# Revit family: NLRS_27_GM_LIB_GI_MR
name_source: partatom
category: Generic Models
revit_build: Autodesk Revit 2017 (Build: 20190507_1515(x64)
units: mm (PartAtom-declared; Revit-internal decimal feet)

## family parameters
Can host rebar = No
Cut with Voids When Loaded = Yes
Part Type = Normal
Room Calculation Point = No
Round Connector Dimension = Use Diameter
Shared = No

## types (18) — shared parameters
01_kraal = No
02_Trim = Yes
03_druppel = Yes
Assembly Code = 27.16
Description = GI Goot
IfcExportAs = IfcFlowsegment
Manufacturer = Meilof Riks
Model = GI
NLRS_C_Binnenbak = RAL 9010
NLRS_C_Materiaal = RAL 9010
Type Image = <None>
URL = https://www.meilofriks.nl
Vorm_Goot_L = 01 : 2_←_Hoek_L
Vorm_Goot_L-R = 01 : 4_↔_Hoek_L-R
Vorm_goot_R = 01 : 3_→_Hoek_R

## per-type parameters (varying)
| type | Breedte_goot | Breedte_goot_hoek | Diepte_bak | Hoogte_AK | Hoogte_VK | Set_Diepte_bak | set_Hoogte_AK |
| GI S280A | 280 mm  [stored 0.918635 ft] | 280 mm  [stored 0.918635 ft] | 87 mm  [stored 0.285433 ft] | 197 mm | 168 mm | 87 mm  [stored 0.285433 ft] | 197 mm |
| GI S310A | 310 mm  [stored 1.01706 ft] | 310 mm  [stored 1.01706 ft] | 74 mm  [stored 0.242782 ft] | 179 mm  [stored 0.58727 ft] | 154 mm  [stored 0.505249 ft] | 74 mm  [stored 0.242782 ft] | 179 mm  [stored 0.58727 ft] |
| GI S365A | 365 mm  [stored 1.19751 ft] | 365 mm  [stored 1.19751 ft] | 95 mm | 204 mm | 176 mm | 95 mm | 204 mm |
| GI S400A | 400 mm  [stored 1.31234 ft] | 400 mm  [stored 1.31234 ft] | 78 mm  [stored 0.255906 ft] | 186 mm  [stored 0.610236 ft] | 157 mm  [stored 0.515092 ft] | 78 mm  [stored 0.255906 ft] | 186 mm  [stored 0.610236 ft] |
| GI S500A | 500 mm  [stored 1.64042 ft] | 500 mm  [stored 1.64042 ft] | 78 mm  [stored 0.255906 ft] | 186 mm  [stored 0.610236 ft] | 157 mm  [stored 0.515092 ft] | 78 mm  [stored 0.255906 ft] | 186 mm  [stored 0.610236 ft] |
| GI S280B | 280 mm  [stored 0.918635 ft] | 280 mm  [stored 0.918635 ft] | 87 mm  [stored 0.285433 ft] | 222 mm | 193 mm | 87 mm  [stored 0.285433 ft] | 222 mm |
| GI S280C | 280 mm  [stored 0.918635 ft] | 280 mm  [stored 0.918635 ft] | 87 mm  [stored 0.285433 ft] | 247 mm | 218 mm | 87 mm  [stored 0.285433 ft] | 247 mm |
| GI S310B | 310 mm  [stored 1.01706 ft] | 310 mm  [stored 1.01706 ft] | 74 mm  [stored 0.242782 ft] | 229 mm | 204 mm | 74 mm  [stored 0.242782 ft] | 229 mm |
| GI S310C | 310 mm  [stored 1.01706 ft] | 310 mm  [stored 1.01706 ft] | 74 mm  [stored 0.242782 ft] | 279 mm | 254 mm | 74 mm  [stored 0.242782 ft] | 279 mm |
| GI S365B | 365 mm  [stored 1.19751 ft] | 365 mm  [stored 1.19751 ft] | 95 mm | 254 mm | 226 mm | 95 mm | 254 mm |
| GI S365C | 365 mm  [stored 1.19751 ft] | 365 mm  [stored 1.19751 ft] | 95 mm | 304 mm | 276 mm | 95 mm | 304 mm |
| GI S400B | 400 mm  [stored 1.31234 ft] | 400 mm  [stored 1.31234 ft] | 78 mm  [stored 0.255906 ft] | 236 mm | 207 mm | 78 mm  [stored 0.255906 ft] | 236 mm |
| GI S400C | 400 mm  [stored 1.31234 ft] | 400 mm  [stored 1.31234 ft] | 78 mm  [stored 0.255906 ft] | 286 mm | 257 mm  [stored 0.843176 ft] | 78 mm  [stored 0.255906 ft] | 286 mm |
| GI S450A | 450 mm | 450 mm | 95 mm | 218 mm | 175 mm | 95 mm | 218 mm |
| GI S450B | 450 mm | 450 mm | 95 mm | 268 mm | 225 mm | 95 mm | 268 mm |
| GI S500B | 500 mm  [stored 1.64042 ft] | 500 mm  [stored 1.64042 ft] | 78 mm  [stored 0.255906 ft] | 236 mm | 207 mm | 78 mm  [stored 0.255906 ft] | 236 mm |
| GI S500C | 500 mm  [stored 1.64042 ft] | 500 mm  [stored 1.64042 ft] | 78 mm  [stored 0.255906 ft] | 286 mm | 257 mm  [stored 0.843176 ft] | 78 mm  [stored 0.255906 ft] | 286 mm |
| GI S450C | 450 mm | 450 mm | 95 mm | 318 mm | 275 mm | 95 mm | 318 mm |

note: [stored X ft] marks values corroborated as IEEE doubles in the binary element streams (Revit-internal decimal feet)

## geometry (parser evidence)
native form markers: Sweep x33
no freeform markers — native parametric forms only
